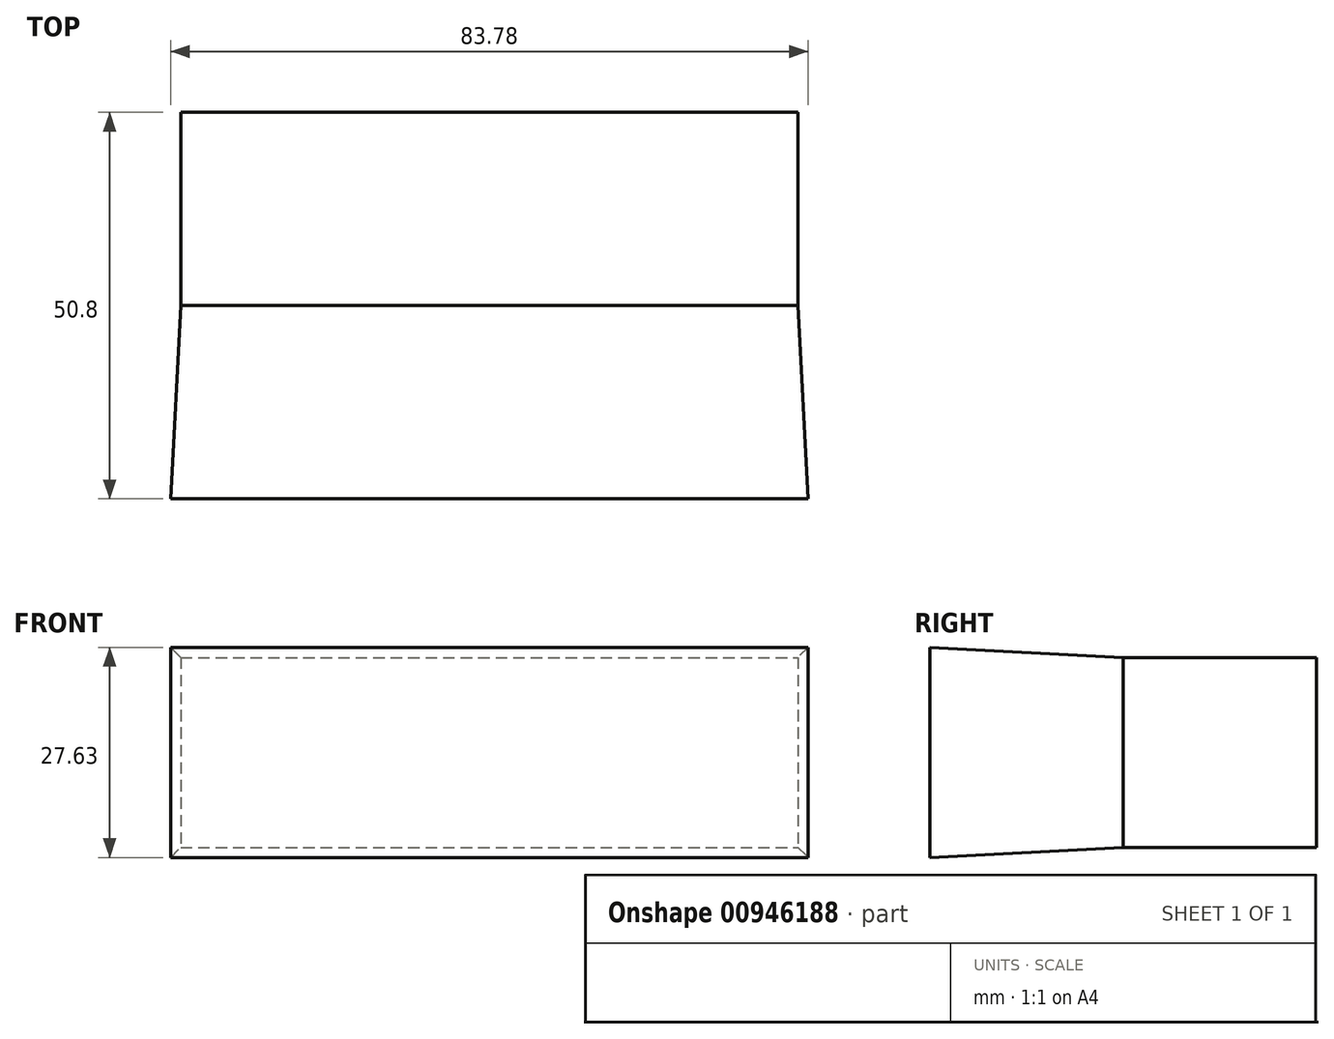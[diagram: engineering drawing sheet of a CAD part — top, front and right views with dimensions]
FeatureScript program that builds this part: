
annotation { "Feature Type Name" : "Feature", "Feature Type Description" : "" }
export const myFeature = defineFeature(function(context is Context, id is Id, definition is map)
    precondition{}
    {
        {
            var Q0;
            Q0=qCreatedBy(makeId("Front.planeOp"),FACE);
            var sketch = newSketch(context, id + "F0", { "sketchPlane" : qUnion([Q0])});
            skLineSegment(sketch, "E0.bottom", {"start": v(-31.87, 47.15) * mm, "end": v(49.25, 47.15) * mm});
            skLineSegment(sketch, "E0.top", {"start": v(-31.87, 22.18) * mm, "end": v(49.25, 22.18) * mm});
            skLineSegment(sketch, "E0.left", {"start": v(-31.87, 47.15) * mm, "end": v(-31.87, 22.18) * mm});
            skLineSegment(sketch, "E0.right", {"start": v(49.25, 47.15) * mm, "end": v(49.25, 22.18) * mm});
            skSolve(sketch);
        }
        {
            var Q0;
            Q0 = qSketchRegion(id + "F0", true);
            extrude(context, id + "F1", {"entities" : qUnion([Q0]), "depth" : 25.4 * mm, "offsetDistance" : 25.4 * mm});
        }
        {
            var Q0;
            Q0=makeQuery(id+"F1.opExtrude","CAP_FACE",FACE,{"disambiguationData":[OSD([sQuery(id+"F0.wireOp",EDGE,"E0.bottom"),sQuery(id+"F0.wireOp",EDGE,"E0.top"),sQuery(id+"F0.wireOp",EDGE,"E0.left"),sQuery(id+"F0.wireOp",EDGE,"E0.right")])],"isStart":false});
            extrude(context, id + "F2", {"entities" : qUnion([Q0]), "operationType" : NewBodyOperationType.ADD, "depth" : 25.4 * mm, "offsetDistance" : 25.4 * mm, "hasDraft" : true, "draftAngle" : 0.05 * radian});
        }
    });
